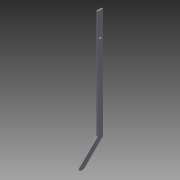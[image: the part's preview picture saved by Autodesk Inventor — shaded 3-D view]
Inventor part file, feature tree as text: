
AUTODESK INVENTOR PART (.ipt)
format: ipt  version: 2013 (Build 170138000, 138)  size: 155,136 bytes
history: native  units: in
note: dims shown in document units (in); Inventor stores cm internally (conversion verified against a paired STEP export)
features: extrude x8, sketch x8
ambient origin geometry x8: Origin, YZ Plane, XZ Plane, XY Plane, X Axis, Y Axis, Z Axis, Center Point
bodies: Solid1 (feature_tree)
feature tree (16):
  extrude  "Extrusion1"  Depth=0.5in
  extrude  "Extrusion2"  Depth=0.5in
  extrude  "Extrusion3"  Depth=16.484in
  extrude  "Extrusion4"  Depth=5.14in
  extrude  "Extrusion5"  Depth=1.0in
  extrude  "Extrusion8"  Depth=6.0in
  extrude  "Extrusion9"  Depth=1.0in
  extrude  "Extrusion10"  Depth=1.0in TaperAngle=0.0deg
  sketch  "Sketch1"  dims[d0=0.25in d1=0.5in]
  sketch  "Sketch2"  dims[d2=0.0in d3=0.5in]
  sketch  "Sketch3"  dims[d4=90.0deg d5=16.484in]
  sketch  "Sketch4"  dims[d6=1.0in d7=5.14in]
  sketch  "Sketch5"  dims[d8=135.0deg d9=1.0in]
  sketch  "Sketch8"  dims[d10=90.0deg d11=6.0in]
  sketch  "Sketch9"  dims[d12=90.0deg d13=1.0in]
  sketch  "Sketch10"  dims[d14=180.0deg d15=1.0in d16=0.0in d17=0.25in d18=0.75in d19=1.0in d20=0.0in d21=5.0in d22=0.0in d23=0.75in d24=0.0in d25=1.0in d26=5.0in d27=5.0in d28=0.0in d43=4.0in d44=0.0in d45=0.5in d46=1.0in d47=0.0in d48=0.4375in d49=0.4375in d50=0.25in d51=0.0in]
